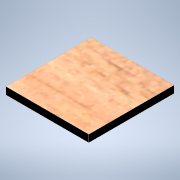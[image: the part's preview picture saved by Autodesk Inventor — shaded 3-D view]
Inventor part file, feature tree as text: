
AUTODESK INVENTOR PART (.ipt)
format: ipt  version: 2021 (Build 250183000, 183)  size: 117,760 bytes
history: native  units: mm
features: extrude x2, sketch x2
ambient origin geometry x8: Origin, YZ Plane, XZ Plane, XY Plane, X Axis, Y Axis, Z Axis, Center Point
bodies: Volumenkörper1 (feature_tree)
feature tree (4):
  extrude  "Extrusion1"  Depth=34.0mm
  extrude  "Extrusion2"  Depth=35.0mm
  sketch  "Skizze1"  dims[d0=35.0mm d1=34.0mm]
  sketch  "Skizze2"  dims[d2=3.0mm d3=0.0mm d4=35.0mm d5=34.0mm d6=3.0mm d7=0.0mm]
